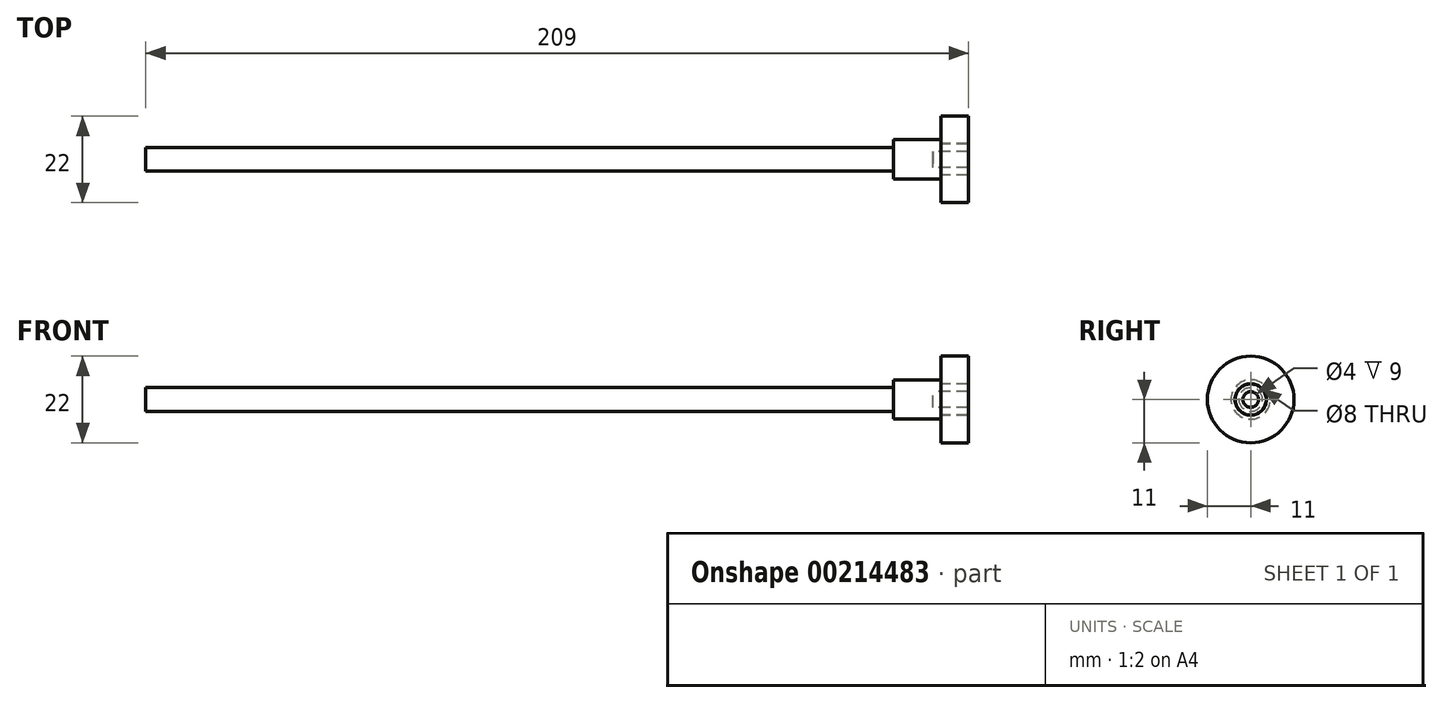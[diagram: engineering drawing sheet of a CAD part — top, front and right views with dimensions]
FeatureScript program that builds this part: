
annotation { "Feature Type Name" : "Feature", "Feature Type Description" : "" }
export const myFeature = defineFeature(function(context is Context, id is Id, definition is map)
    precondition{}
    {
        {
            var Q0;
            Q0=qCreatedBy(makeId("Right.planeOp"),FACE);
            var sketch = newSketch(context, id + "F0", { "sketchPlane" : qUnion([Q0])});
            skCircle(sketch, "E0", {"center": v(0, 0) * mm, "radius": 3 * mm});
            skSolve(sketch);
        }
        {
            var Q0;
            Q0=makeQuery(id+"F0.imprint","IMPRINT",FACE,{"disambiguationData":[TD([[makeQuery(id+"F0.imprint","IMPRINT",EDGE,{"derivedFrom":sQuery(id+"F0.wireOp",EDGE,"E0")}),1.0]])]});
            extrude(context, id + "F1", {"entities" : qUnion([Q0]), "depth" : 200 * mm});
        }
        {
            var Q0;
            Q0=makeQuery(id+"F1.opExtrude","CAP_FACE",FACE,{"disambiguationData":[OSD([sQuery(id+"F0.wireOp",EDGE,"E0")])],"isStart":false});
            var sketch = newSketch(context, id + "F2", { "sketchPlane" : qUnion([Q0])});
            skCircle(sketch, "E1", {"center": v(0, 0) * mm, "radius": 2 * mm});
            skCircle(sketch, "E2", {"center": v(0, 0) * mm, "radius": 5 * mm});
            skCircle(sketch, "E3", {"center": v(0, 0) * mm, "radius": 2.95 * mm});
            skSolve(sketch);
        }
        {
            var Q0;
            Q0=makeQuery(id+"F2.imprint","IMPRINT",FACE,{"disambiguationData":[TD([[makeQuery(id+"F2.imprint","IMPRINT",EDGE,{"derivedFrom":sQuery(id+"F2.wireOp",EDGE,"E1")}),-1.0]])]});
            var Q1;
            Q1=makeQuery(id+"F2.imprint","IMPRINT",FACE,{"disambiguationData":[TD([[makeQuery(id+"F2.imprint","IMPRINT",EDGE,{"derivedFrom":sQuery(id+"F2.wireOp",EDGE,"E2")}),1.0]])]});
            var Q2;
            Q2=makeQuery(id+"F2.imprint","IMPRINT",FACE,{"disambiguationData":[TD([[makeQuery(id+"F2.imprint","IMPRINT",EDGE,{"derivedFrom":sQuery(id+"F2.wireOp",EDGE,"E3")}),-1.0]])]});
            extrude(context, id + "F3", {"entities" : qUnion([Q0, Q1, Q2]), "depth" : 2 * mm});
        }
        {
            var Q0;
            Q0=makeQuery(id+"F2.imprint","IMPRINT",FACE,{"disambiguationData":[TD([[makeQuery(id+"F2.imprint","IMPRINT",EDGE,{"derivedFrom":sQuery(id+"F2.wireOp",EDGE,"E3")}),-1.0]])]});
            var Q1;
            Q1=makeQuery(id+"F2.imprint","IMPRINT",FACE,{"disambiguationData":[TD([[makeQuery(id+"F2.imprint","IMPRINT",EDGE,{"derivedFrom":sQuery(id+"F2.wireOp",EDGE,"E2")}),1.0]])]});
            extrude(context, id + "F4", {"entities" : qUnion([Q0, Q1]), "operationType" : NewBodyOperationType.ADD, "oppositeDirection" : true, "depth" : 10 * mm});
        }
        {
            var Q0;
            Q0=makeQuery(id+"F3.opExtrude","CAP_FACE",FACE,{"disambiguationData":[OSD([sQuery(id+"F2.wireOp",EDGE,"E1"),sQuery(id+"F2.wireOp",EDGE,"E2")])],"isStart":false});
            var sketch = newSketch(context, id + "F5", { "sketchPlane" : qUnion([Q0])});
            skCircle(sketch, "E4", {"center": v(0, 0) * mm, "radius": 3.95 * mm});
            skCircle(sketch, "E5", {"center": v(0, 0) * mm, "radius": 2 * mm});
            skSolve(sketch);
        }
        {
            var Q0;
            Q0=makeQuery(id+"F5.imprint","IMPRINT",FACE,{"disambiguationData":[TD([[makeQuery(id+"F5.imprint","IMPRINT",EDGE,{"derivedFrom":sQuery(id+"F5.wireOp",EDGE,"E4")}),1.0]])]});
            extrude(context, id + "F6", {"entities" : qUnion([Q0]), "operationType" : NewBodyOperationType.ADD, "depth" : 7 * mm});
        }
        {
            var Q0;
            Q0=makeQuery(id+"F3.opExtrude","CAP_FACE",FACE,{"disambiguationData":[OSD([sQuery(id+"F2.wireOp",EDGE,"E1"),sQuery(id+"F2.wireOp",EDGE,"E2")])],"isStart":false});
            var sketch = newSketch(context, id + "F7", { "sketchPlane" : qUnion([Q0])});
            skCircle(sketch, "E6", {"center": v(0, 0) * mm, "radius": 4 * mm});
            skCircle(sketch, "E7", {"center": v(0, 0) * mm, "radius": 11 * mm});
            skSolve(sketch);
        }
        {
            var Q0;
            Q0=makeQuery(id+"F7.imprint","IMPRINT",FACE,{"disambiguationData":[TD([[makeQuery(id+"F7.imprint","IMPRINT",EDGE,{"derivedFrom":sQuery(id+"F7.wireOp",EDGE,"E6")}),-1.0]])]});
            var Q1;
            Q1=makeQuery(id+"F7.imprint","IMPRINT",FACE,{"disambiguationData":[TD([[makeQuery(id+"F7.imprint","IMPRINT",EDGE,{"derivedFrom":sQuery(id+"F7.wireOp",EDGE,"E7")}),1.0]])]});
            extrude(context, id + "F8", {"entities" : qUnion([Q0, Q1]), "depth" : 7 * mm});
        }
    });
